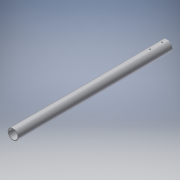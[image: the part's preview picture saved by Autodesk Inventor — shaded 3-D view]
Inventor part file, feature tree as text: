
AUTODESK INVENTOR PART (.ipt)
format: ipt  version: 2016 (Build 200138000, 138)  size: 117,760 bytes
history: native  units: in
note: dims shown in document units (in); Inventor stores cm internally (conversion verified against a paired STEP export)
features: sketch x4, extrude x2, hole x2
ambient origin geometry x8: Origin, YZ Plane, XZ Plane, XY Plane, X Axis, Y Axis, Z Axis, Center Point
bodies: Solid1 (feature_tree)
feature tree (8):
  extrude  "Extrusion1"  Depth=0.0638in
  extrude  "Extrusion3"  Depth=0.4134in
  hole  "Hole4"  [1 undecoded]
  hole  "Hole5"  [1 undecoded]
  sketch  "Sketch1"  dims[d0=0.8661in d2=0.0638in]
  sketch  "Sketch6"  dims[d3=12.5984in d4=0.0in d18=0.4134in]
  sketch  "Sketch8"  dims[d19=1.0in d20=0.0in d47=0.3937in]
  sketch  "Sketch9"  dims[d48=0.1181in d49=0.2362in d50=0.1575in d51=0.0787in d52=90.0deg d53=0.315in d54=0.8108in d55=0.9843in d56=0.1181in d57=0.2362in d58=0.1575in d59=0.0787in d60=90.0deg d61=0.315in d62=0.8108in]
note: 2 required parameter values undecoded (feature->parameter linkage not recoverable at this tier; creation-order binding heuristic only, values carry confidence <= 0.55)
